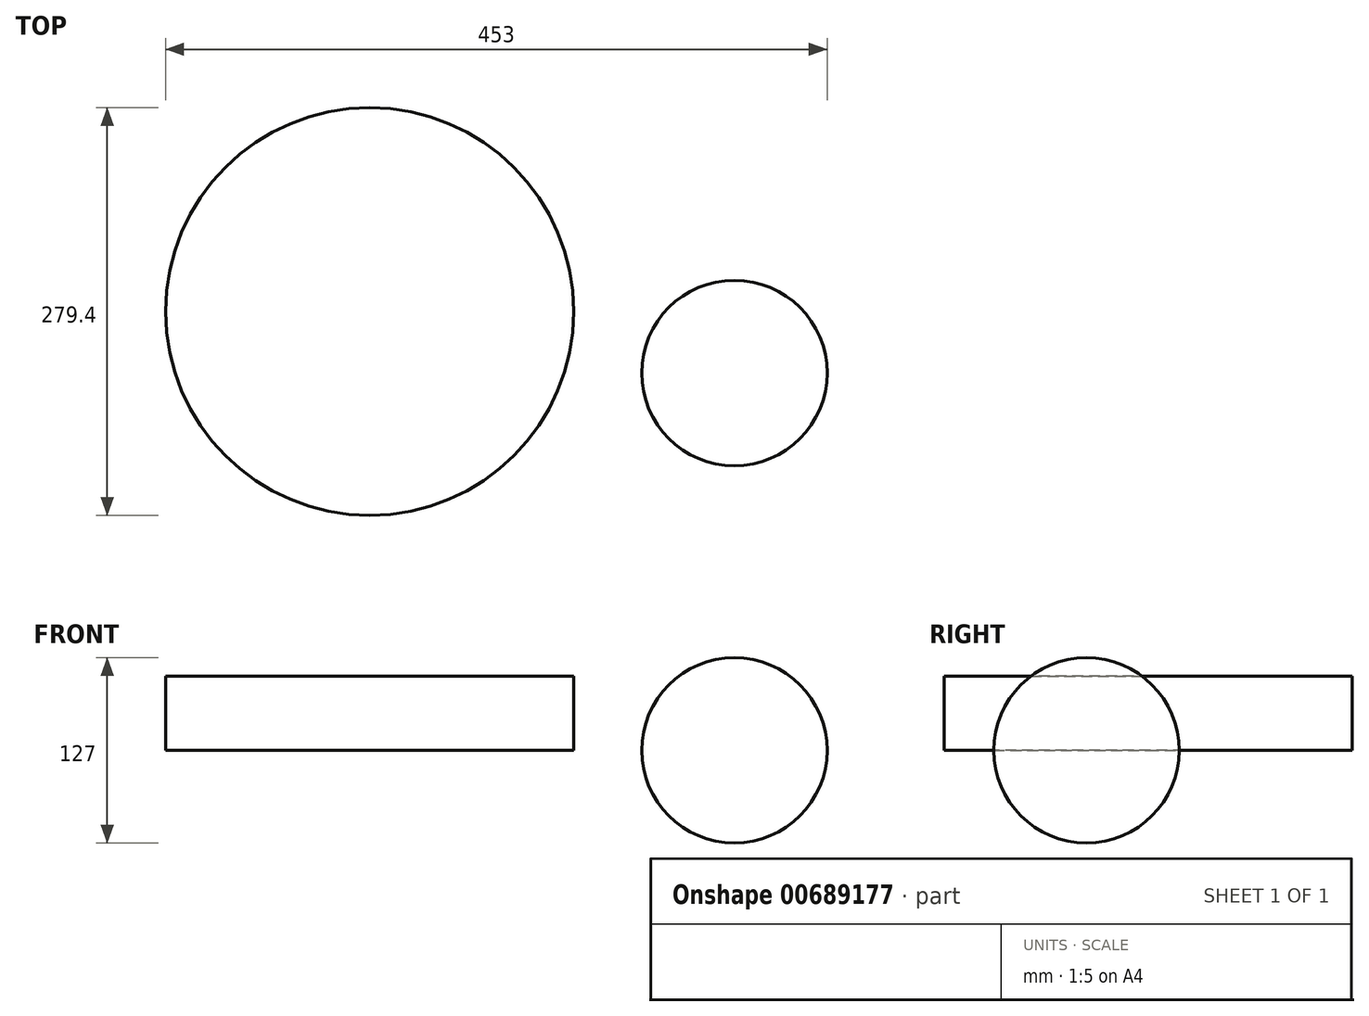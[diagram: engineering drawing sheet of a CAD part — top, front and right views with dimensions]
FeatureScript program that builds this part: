
annotation { "Feature Type Name" : "Feature", "Feature Type Description" : "" }
export const myFeature = defineFeature(function(context is Context, id is Id, definition is map)
    precondition{}
    {
        {
            var Q0;
            Q0=qCreatedBy(makeId("Top.planeOp"),FACE);
            var sketch = newSketch(context, id + "F0", { "sketchPlane" : qUnion([Q0])});
            skCircle(sketch, "E0", {"center": v(-44.84, 35.38) * mm, "radius": 139.7 * mm});
            skSolve(sketch);
        }
        {
            var Q0;
            Q0=makeQuery(id+"F0.imprint","IMPRINT",FACE,{"disambiguationData":[TD([[makeQuery(id+"F0.imprint","IMPRINT",EDGE,{"derivedFrom":sQuery(id+"F0.wireOp",EDGE,"E0")}),1.0]])]});
            extrude(context, id + "F1", {"entities" : qUnion([Q0]), "depth" : 50.8 * mm, "offsetDistance" : 25.4 * mm});
        }
        {
            var Q0;
            Q0=qCreatedBy(makeId("Top.planeOp"),FACE);
            var sketch = newSketch(context, id + "F2", { "sketchPlane" : qUnion([Q0])});
            skArc(sketch, "E1", {"start": v(268.46, -6.76) * mm, "mid": v(204.96, 56.74) * mm, "end": v(141.46, -6.76) * mm});
            skLineSegment(sketch, "E2", {"start": v(141.46, -6.76) * mm, "end": v(268.46, -6.76) * mm});
            skSolve(sketch);
        }
        {
            var Q0;
            Q0=makeQuery(id+"F2.imprint","IMPRINT",FACE,{"disambiguationData":[TD([[makeQuery(id+"F2.imprint","IMPRINT",EDGE,{"derivedFrom":sQuery(id+"F2.wireOp",EDGE,"E1")}),1.0]])]});
            var Q1;
            Q1=sQuery(id+"F2.wireOp",EDGE,"E2");
            revolve(context, id + "F3", {"entities" : qUnion([Q0]), "axis" : qUnion([Q1]), "revolveType" : RevolveType.FULL});
        }
    });
